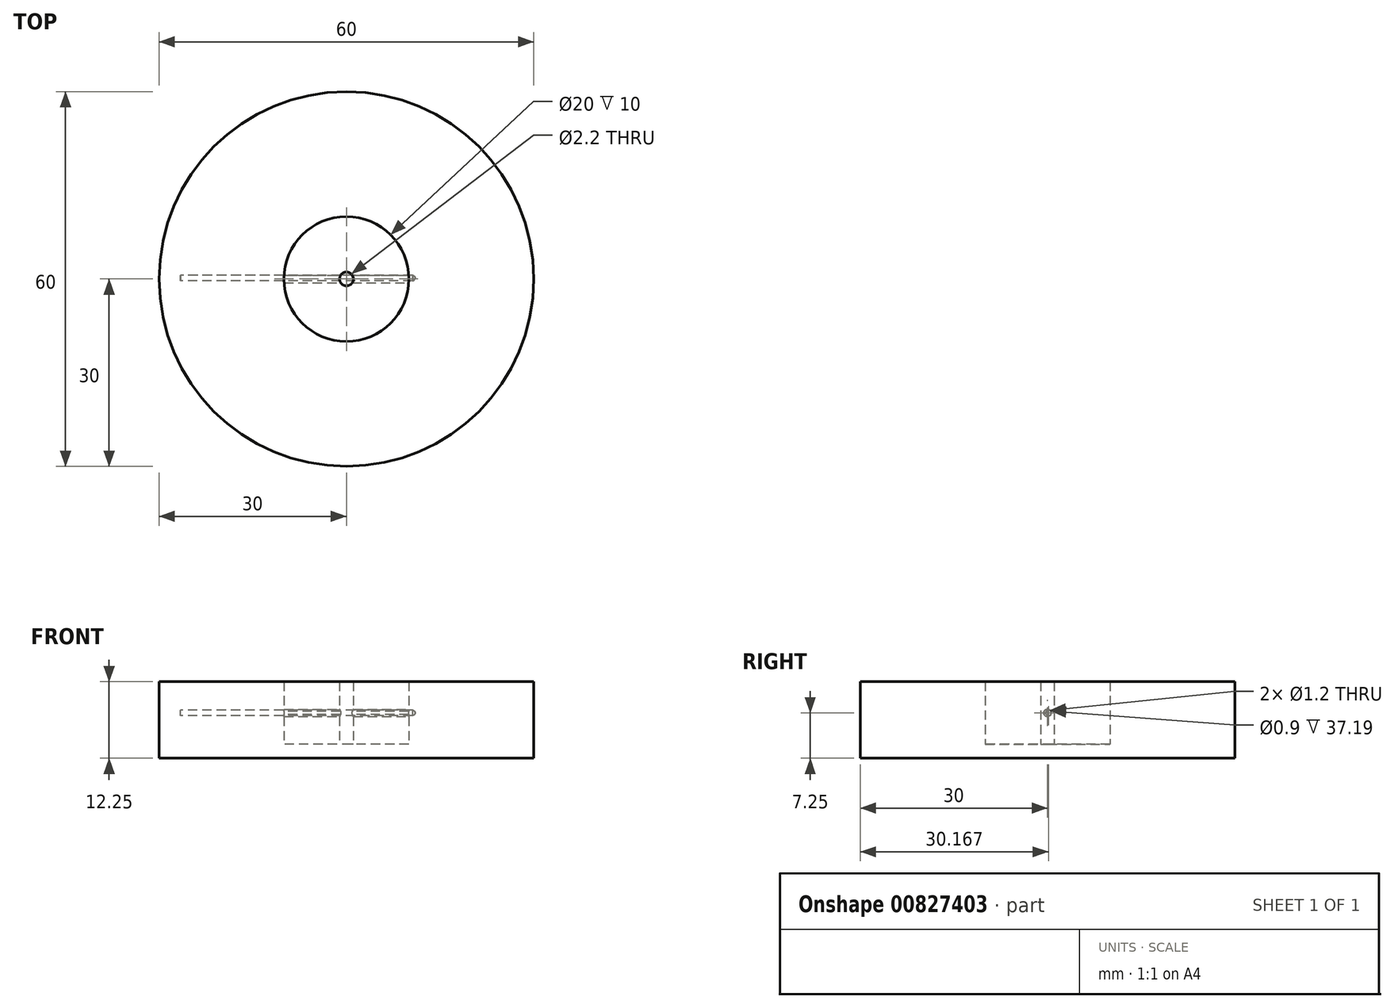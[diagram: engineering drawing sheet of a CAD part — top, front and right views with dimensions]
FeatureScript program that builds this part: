
annotation { "Feature Type Name" : "Feature", "Feature Type Description" : "" }
export const myFeature = defineFeature(function(context is Context, id is Id, definition is map)
    precondition{}
    {
        {
            var Q0;
            Q0=qCreatedBy(makeId("Top.planeOp"),FACE);
            var sketch = newSketch(context, id + "F0", { "sketchPlane" : qUnion([Q0])});
            skCircle(sketch, "E0", {"center": v(0, 0) * mm, "radius": 10 * mm});
            skCircle(sketch, "E1", {"center": v(0, 0) * mm, "radius": 1.1 * mm});
            skSolve(sketch);
        }
        {
            var Q0;
            Q0=makeQuery(id+"F0.imprint","IMPRINT",FACE,{"disambiguationData":[TD([[makeQuery(id+"F0.imprint","IMPRINT",EDGE,{"derivedFrom":sQuery(id+"F0.wireOp",EDGE,"E0")}),1.0]])]});
            extrude(context, id + "F1", {"entities" : qUnion([Q0]), "depth" : 10 * mm, "offsetDistance" : 25 * mm});
        }
        {
            var Q0;
            Q0=qCreatedBy(makeId("Right.planeOp"),FACE);
            var sketch = newSketch(context, id + "F2", { "sketchPlane" : qUnion([Q0])});
            skLineSegment(sketch, "E2", {"start": v(-10, 0) * mm, "end": v(-10, 10) * mm});
            skLineSegment(sketch, "E3", {"start": v(10, 10) * mm, "end": v(10, 0) * mm});
            skLineSegment(sketch, "E4.0", {"start": v(-10, 10) * mm, "end": v(10, 10) * mm});
            skLineSegment(sketch, "E5.0", {"start": v(-10, 0) * mm, "end": v(10, 0) * mm});
            skLineSegment(sketch, "E6", {"start": v(-10, 5) * mm, "end": v(10, 5) * mm, "construction": true});
            skLineSegment(sketch, "E7", {"start": v(0, 10) * mm, "end": v(0, 0) * mm, "construction": true});
            skCircle(sketch, "E8", {"center": v(0, 5) * mm, "radius": 0.6 * mm});
            skSolve(sketch);
        }
        {
            var Q0;
            Q0=makeQuery(id+"F2.imprint","IMPRINT",FACE,{"disambiguationData":[TD([[makeQuery(id+"F2.imprint","IMPRINT",EDGE,{"derivedFrom":sQuery(id+"F2.wireOp",EDGE,"E8")}),1.0]])]});
            extrude(context, id + "F3", {"entities" : qUnion([Q0]), "operationType" : NewBodyOperationType.REMOVE, "oppositeDirection" : true, "depth" : 25 * mm, "offsetDistance" : 25 * mm, "hasSecondDirection" : true, "secondDirectionOppositeDirection" : false, "secondDirectionDepth" : 25 * mm});
        }
        {
            var Q0;
            Q0=makeQuery(id+"F2.imprint","IMPRINT",FACE,{"disambiguationData":[TD([[makeQuery(id+"F2.imprint","IMPRINT",EDGE,{"derivedFrom":sQuery(id+"F2.wireOp",EDGE,"E2")}),-1.0]])]});
            var sketch = newSketch(context, id + "F4", { "sketchPlane" : qUnion([Q0])});
            skCircle(sketch, "E9.0", {"center": v(0, 5) * mm, "radius": 0.6 * mm});
            skCircle(sketch, "E10", {"center": v(0.17, 5) * mm, "radius": 0.45 * mm});
            skLineSegment(sketch, "E11", {"start": v(0, 5) * mm, "end": v(0.6, 5) * mm, "construction": true});
            skSolve(sketch);
        }
        {
            var Q0;
            Q0=makeQuery(id+"F4.imprint","IMPRINT",FACE,{"disambiguationData":[TD([[makeQuery(id+"F4.imprint","IMPRINT",EDGE,{"derivedFrom":sQuery(id+"F4.wireOp",EDGE,"E10")}),1.0]])]});
            extrude(context, id + "F5", {"entities" : qUnion([Q0]), "depth" : 11 * mm, "offsetDistance" : 25 * mm, "hasSecondDirection" : true, "secondDirectionOppositeDirection" : true, "secondDirectionDepth" : 26.59 * mm});
        }
        {
            var Q0;
            Q0=makeQuery(id+"F5.opExtrude","CAP_EDGE",EDGE,{"disambiguationData":[OSD([sQuery(id+"F4.wireOp",EDGE,"E10")])],"isStart":false});
            fillet(context, id + "F6", {"entities" : qUnion([Q0]), "radius" : 0.4 * mm, "tangentPropagation" : true, "rho" : 0.3, "crossSection" : FilletCrossSection.CONIC, "allowEdgeOverflow" : false});
        }
        {
            var Q0;
            Q0=qCreatedBy(makeId("Top.planeOp"),FACE);
            var sketch = newSketch(context, id + "F7", { "sketchPlane" : qUnion([Q0])});
            skCircle(sketch, "E12", {"center": v(0, 0) * mm, "radius": 30 * mm});
            skSolve(sketch);
        }
        {
            var Q0;
            Q0=makeQuery(id+"F7.imprint","IMPRINT",FACE,{"disambiguationData":[TD([[makeQuery(id+"F7.imprint","IMPRINT",EDGE,{"derivedFrom":sQuery(id+"F7.wireOp",EDGE,"E12")}),1.0]])]});
            extrude(context, id + "F8", {"entities" : qUnion([Q0]), "depth" : 10 * mm, "offsetDistance" : 25 * mm, "hasSecondDirection" : true, "secondDirectionOppositeDirection" : true, "secondDirectionDepth" : 2.25 * mm});
        }
        {
            var Q0;
            Q0=makeQuery(id+"F8.opExtrude","SWEPT_BODY",BODY,{"disambiguationData":[OSD([sQuery(id+"F7.wireOp",EDGE,"E12")])]});
            transform(context, id + "F9", {"entities" : qUnion([Q0]), "transformType" : TransformType.TRANSLATION_3D, "dx" : 0 * mm, "dy" : 0 * mm, "dz" : 0 * mm, "makeCopy" : true});
        }
        {
            var Q0;
            Q0=makeQuery(id+"F9.opPattern","COPY",BODY,{"derivedFrom":makeQuery(id+"F8.opExtrude","SWEPT_BODY",BODY,{"disambiguationData":[OSD([sQuery(id+"F7.wireOp",EDGE,"E12")])]}),"instanceName":"1"});
            deleteBodies(context, id + "F10", {"entities" : qUnion([Q0])});
        }
        {
            var Q0;
            Q0=makeQuery(id+"F1.opExtrude","SWEPT_BODY",BODY,{"disambiguationData":[OSD([sQuery(id+"F0.wireOp",EDGE,"E0"),sQuery(id+"F0.wireOp",EDGE,"E1")])]});
            var Q1;
            Q1=makeQuery(id+"F5.opExtrude","SWEPT_BODY",BODY,{"disambiguationData":[OSD([sQuery(id+"F4.wireOp",EDGE,"E10")])]});
            var Q2;
            Q2=makeQuery(id+"F8.opExtrude","SWEPT_BODY",BODY,{"disambiguationData":[OSD([sQuery(id+"F7.wireOp",EDGE,"E12")])]});
            booleanBodies(context, id + "F11", {"operationType" : BooleanOperationType.SUBTRACTION, "tools" : qUnion([Q0, Q1]), "targets" : qUnion([Q2]), "keepTools" : true});
        }
    });
